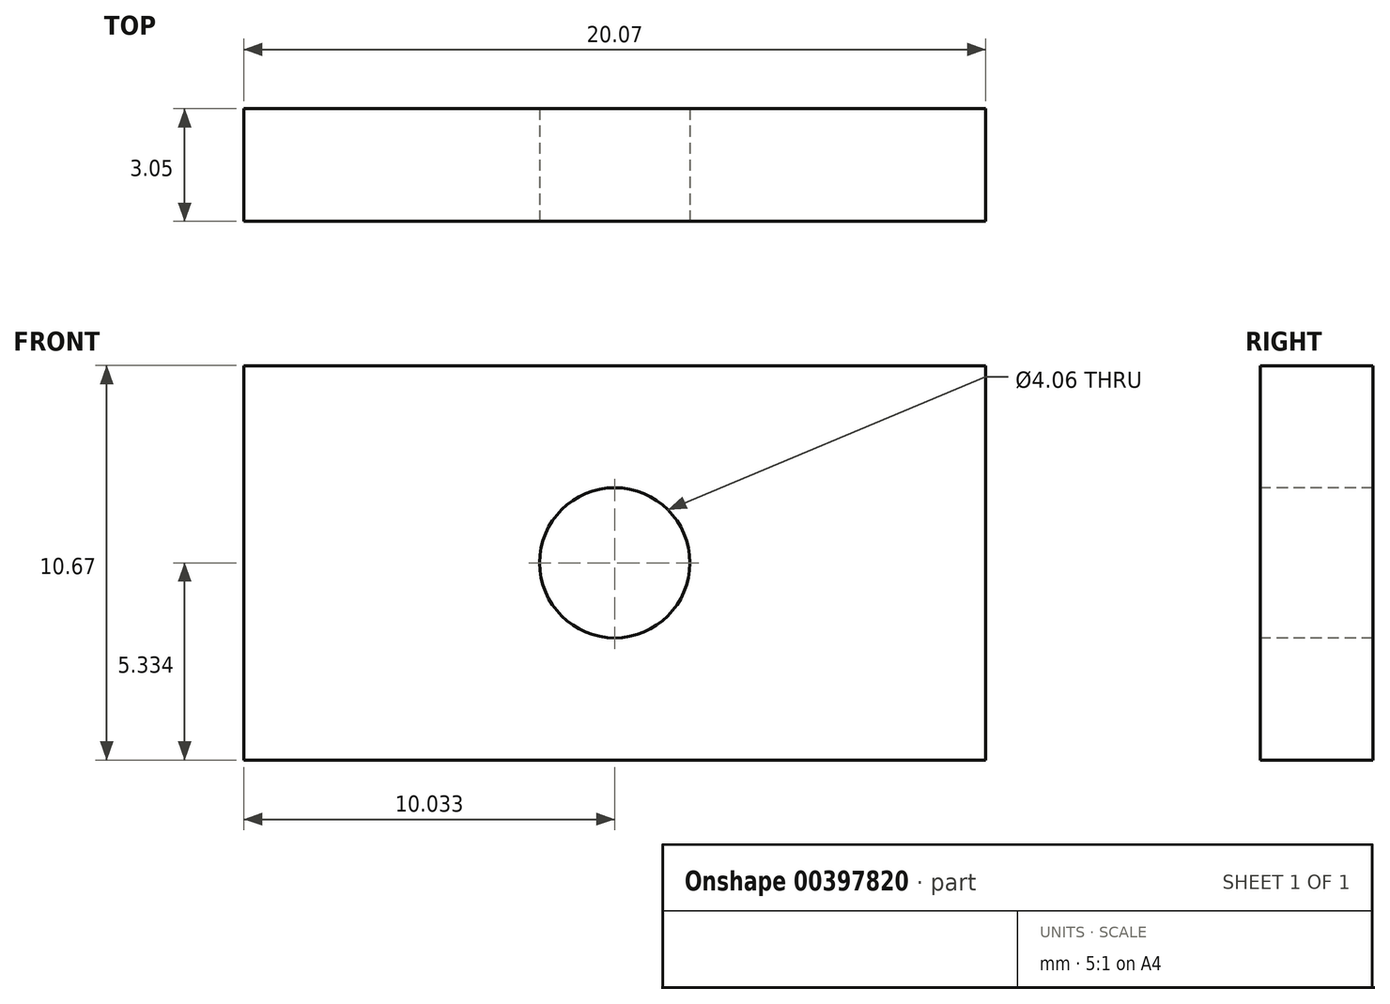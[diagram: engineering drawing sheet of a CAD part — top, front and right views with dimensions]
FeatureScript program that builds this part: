
annotation { "Feature Type Name" : "Feature", "Feature Type Description" : "" }
export const myFeature = defineFeature(function(context is Context, id is Id, definition is map)
    precondition{}
    {
        {
            var Q0;
            Q0=qCreatedBy(makeId("Front.planeOp"),FACE);
            var sketch = newSketch(context, id + "F0", { "sketchPlane" : qUnion([Q0])});
            skLineSegment(sketch, "E0.bottom", {"start": v(0, 0) * mm, "end": v(20.07, 0) * mm});
            skLineSegment(sketch, "E0.top", {"start": v(0, 10.67) * mm, "end": v(20.07, 10.67) * mm});
            skLineSegment(sketch, "E0.left", {"start": v(0, 0) * mm, "end": v(0, 10.67) * mm});
            skLineSegment(sketch, "E0.right", {"start": v(20.07, 0) * mm, "end": v(20.07, 10.67) * mm});
            skSolve(sketch);
        }
        {
            var Q0;
            Q0 = qSketchRegion(id + "F0", true);
            extrude(context, id + "F1", {"entities" : qUnion([Q0]), "depth" : 3.05 * mm});
        }
        {
            var Q0;
            Q0=makeQuery(id+"F1.opExtrude","CAP_FACE",FACE,{"disambiguationData":[OSD([sQuery(id+"F0.wireOp",EDGE,"E0.bottom"),sQuery(id+"F0.wireOp",EDGE,"E0.top"),sQuery(id+"F0.wireOp",EDGE,"E0.left"),sQuery(id+"F0.wireOp",EDGE,"E0.right")])],"isStart":false});
            var sketch = newSketch(context, id + "F2", { "sketchPlane" : qUnion([Q0])});
            skCircle(sketch, "E1", {"center": v(10.03, 5.33) * mm, "radius": 2.03 * mm});
            skLineSegment(sketch, "E2", {"start": v(10.03, 10.67) * mm, "end": v(10.03, 0) * mm, "construction": true});
            skLineSegment(sketch, "E3", {"start": v(0, 5.33) * mm, "end": v(20.07, 5.33) * mm, "construction": true});
            skSolve(sketch);
        }
        {
            var Q0;
            Q0 = qSketchRegion(id + "F2", true);
            extrude(context, id + "F3", {"entities" : qUnion([Q0]), "operationType" : NewBodyOperationType.REMOVE, "endBound" : BoundingType.THROUGH_ALL, "oppositeDirection" : true, "depth" : 25.4 * mm});
        }
    });
